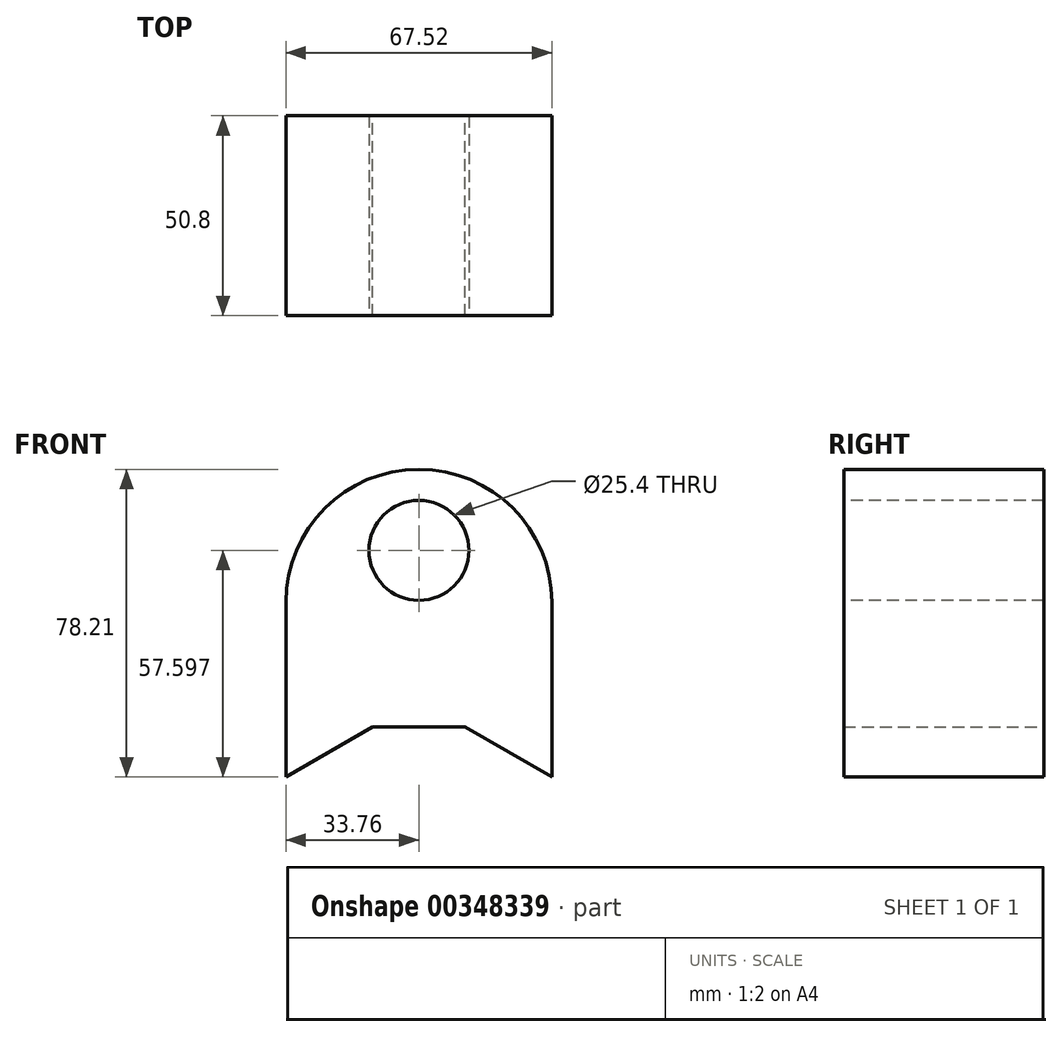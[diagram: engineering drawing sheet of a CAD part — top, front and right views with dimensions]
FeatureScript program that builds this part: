
annotation { "Feature Type Name" : "Feature", "Feature Type Description" : "" }
export const myFeature = defineFeature(function(context is Context, id is Id, definition is map)
    precondition{}
    {
        {
            var Q0;
            Q0=qCreatedBy(makeId("Front.planeOp"),FACE);
            var sketch = newSketch(context, id + "F0", { "sketchPlane" : qUnion([Q0])});
            skLineSegment(sketch, "E0.top", {"start": v(33.76, -22.22) * mm, "end": v(-33.76, -22.22) * mm});
            skLineSegment(sketch, "E0.left", {"start": v(33.76, 22.23) * mm, "end": v(33.76, -22.23) * mm});
            skLineSegment(sketch, "E0.right", {"start": v(-33.76, 22.23) * mm, "end": v(-33.76, -22.22) * mm});
            skPoint(sketch, "E0.middle", {"position": v(0, 0) * mm});
            skArc(sketch, "E1", {"start": v(33.76, 22.23) * mm, "mid": v(0, 55.98) * mm, "end": v(-33.76, 22.23) * mm});
            skLineSegment(sketch, "E2", {"start": v(-33.76, -22.22) * mm, "end": v(-11.76, -9.52) * mm});
            skLineSegment(sketch, "E3", {"start": v(-11.76, -9.52) * mm, "end": v(11.76, -9.52) * mm});
            skLineSegment(sketch, "E4", {"start": v(11.76, -9.52) * mm, "end": v(33.76, -22.22) * mm});
            skSolve(sketch);
        }
        {
            var Q0;
            Q0=makeQuery(id+"F0.imprint","IMPRINT",FACE,{"disambiguationData":[TD([[makeQuery(id+"F0.imprint","IMPRINT",EDGE,{"derivedFrom":sQuery(id+"F0.wireOp",EDGE,"E0.left")}),-1.0]])]});
            extrude(context, id + "F1", {"entities" : qUnion([Q0]), "endBound" : BoundingType.SYMMETRIC, "depth" : 50.8 * mm});
        }
        {
            var Q0;
            Q0=makeQuery(id+"F1.opExtrude","CAP_FACE",FACE,{"disambiguationData":[OSD([sQuery(id+"F0.wireOp",EDGE,"E0.left"),sQuery(id+"F0.wireOp",EDGE,"E0.right"),sQuery(id+"F0.wireOp",EDGE,"E1"),sQuery(id+"F0.wireOp",EDGE,"E2"),sQuery(id+"F0.wireOp",EDGE,"E3"),sQuery(id+"F0.wireOp",EDGE,"E4")])],"isStart":false});
            var sketch = newSketch(context, id + "F2", { "sketchPlane" : qUnion([Q0])});
            skCircle(sketch, "E5", {"center": v(0, 35.37) * mm, "radius": 12.7 * mm});
            skSolve(sketch);
        }
        {
            var Q0;
            Q0=sQuery(id+"F2.wireOp",VERTEX,"E5.center");
            var Q1;
            Q1=makeQuery(id+"F1.opExtrude","SWEPT_BODY",BODY,{"disambiguationData":[OSD([sQuery(id+"F0.wireOp",EDGE,"E0.left"),sQuery(id+"F0.wireOp",EDGE,"E0.right"),sQuery(id+"F0.wireOp",EDGE,"E1"),sQuery(id+"F0.wireOp",EDGE,"E2"),sQuery(id+"F0.wireOp",EDGE,"E3"),sQuery(id+"F0.wireOp",EDGE,"E4")])]});
            hole(context, id + "F3", {"style" : HoleStyle.SIMPLE, "endStyle" : HoleEndStyle.BLIND, "holeDiameter" : 25.4 * mm, "holeDepth" : 76.2 * mm, "isTappedThrough" : true, "tappedDepth" : 12.7 * mm, "tapClearance" : 3, "locations" : qUnion([Q0]), "scope" : qUnion([Q1])});
        }
    });
